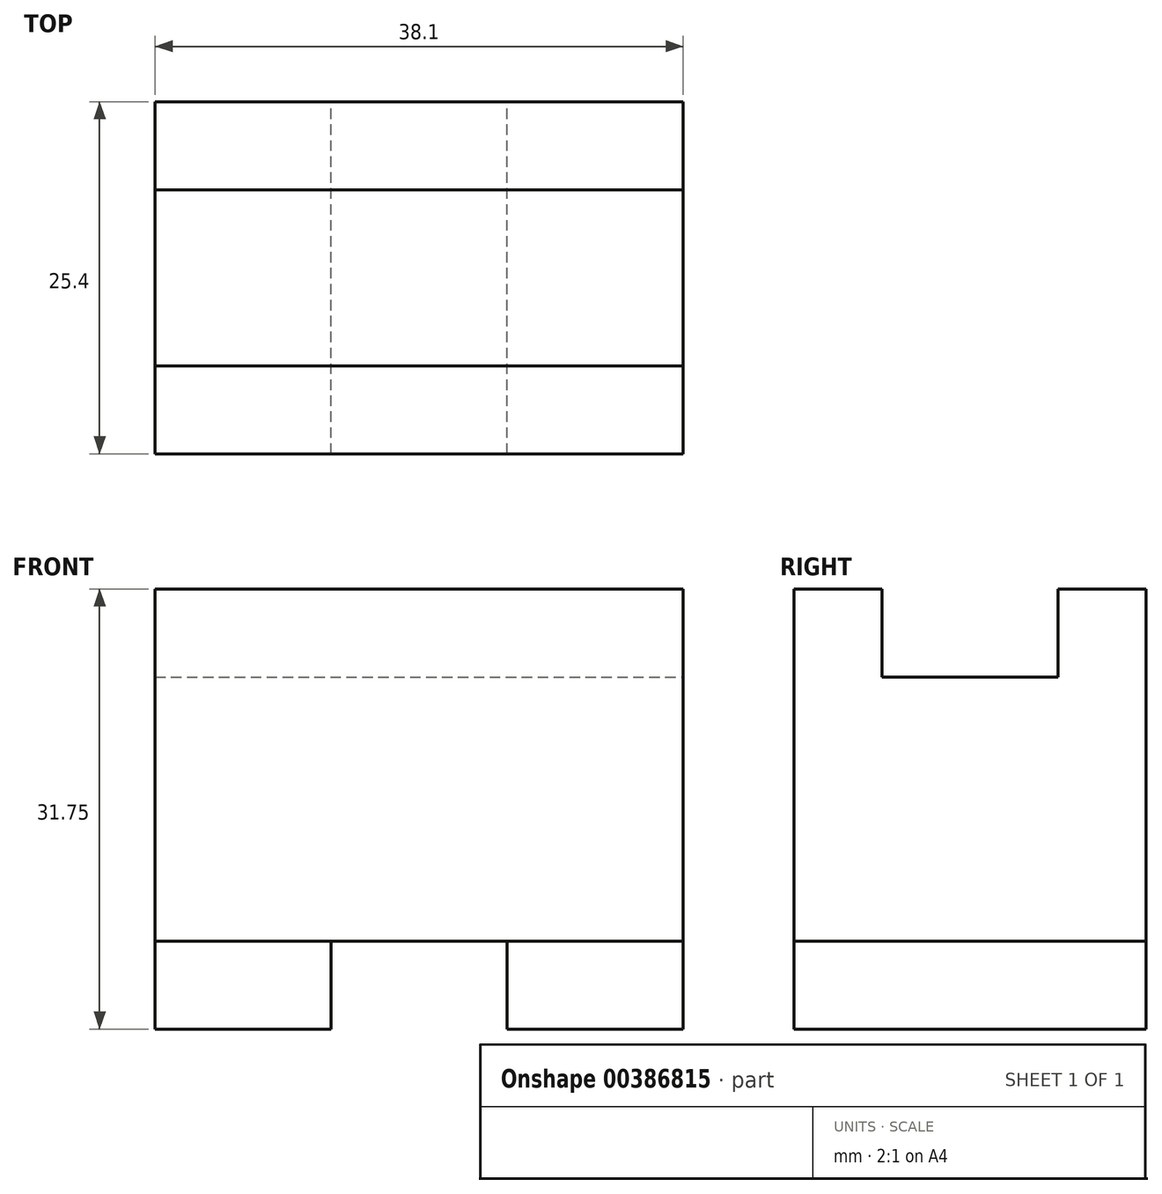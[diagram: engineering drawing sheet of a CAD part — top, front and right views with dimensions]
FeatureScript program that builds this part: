
annotation { "Feature Type Name" : "Feature", "Feature Type Description" : "" }
export const myFeature = defineFeature(function(context is Context, id is Id, definition is map)
    precondition{}
    {
        {
            var Q0;
            Q0=qCreatedBy(makeId("Top.planeOp"),FACE);
            var sketch = newSketch(context, id + "F0", { "sketchPlane" : qUnion([Q0])});
            skLineSegment(sketch, "E0", {"start": v(0, 0) * mm, "end": v(38.1, 0) * mm});
            skLineSegment(sketch, "E1", {"start": v(38.1, 0) * mm, "end": v(38.1, 25.4) * mm});
            skLineSegment(sketch, "E2", {"start": v(38.1, 25.4) * mm, "end": v(0, 25.4) * mm});
            skLineSegment(sketch, "E3", {"start": v(0, 25.4) * mm, "end": v(0, 0) * mm});
            skLineSegment(sketch, "E4", {"start": v(38.1, 0) * mm, "end": v(25.4, 0) * mm});
            skLineSegment(sketch, "E5", {"start": v(25.4, 0) * mm, "end": v(25.4, 25.4) * mm});
            skLineSegment(sketch, "E6", {"start": v(25.4, 25.4) * mm, "end": v(38.1, 25.4) * mm});
            skLineSegment(sketch, "E7", {"start": v(0, 0) * mm, "end": v(12.7, 0) * mm});
            skLineSegment(sketch, "E8", {"start": v(12.7, 0) * mm, "end": v(12.7, 25.4) * mm});
            skLineSegment(sketch, "E9", {"start": v(12.7, 25.4) * mm, "end": v(0, 25.4) * mm});
            skSolve(sketch);
        }
        {
            var Q0;
            Q0=makeQuery(id+"F0.imprint","IMPRINT",FACE,{"disambiguationData":[TD([[makeQuery(id+"F0.imprint","IMPRINT",EDGE,{"derivedFrom":sQuery(id+"F0.wireOp",EDGE,"E1")}),1.0]])]});
            var Q1;
            Q1=makeQuery(id+"F0.imprint","IMPRINT",FACE,{"disambiguationData":[TD([[makeQuery(id+"F0.imprint","IMPRINT",EDGE,{"derivedFrom":sQuery(id+"F0.wireOp",EDGE,"E3")}),1.0]])]});
            extrude(context, id + "F1", {"entities" : qUnion([Q0, Q1]), "depth" : 6.35 * mm});
        }
        {
            var Q0;
            Q0=qCreatedBy(makeId("Top.planeOp"),FACE);
            var sketch = newSketch(context, id + "F2", { "sketchPlane" : qUnion([Q0])});
            skLineSegment(sketch, "E10", {"start": v(0, 0) * mm, "end": v(38.1, 0) * mm});
            skLineSegment(sketch, "E11", {"start": v(38.1, 0) * mm, "end": v(38.1, 25.4) * mm});
            skLineSegment(sketch, "E12", {"start": v(38.1, 25.4) * mm, "end": v(0, 25.4) * mm});
            skLineSegment(sketch, "E13", {"start": v(0, 25.4) * mm, "end": v(0, 0) * mm});
            skSolve(sketch);
        }
        {
            var Q0;
            Q0=makeQuery(id+"F1.opExtrude","CAP_FACE",FACE,{"disambiguationData":[OSD([sQuery(id+"F0.wireOp",EDGE,"E3"),sQuery(id+"F0.wireOp",EDGE,"E7"),sQuery(id+"F0.wireOp",EDGE,"E8"),sQuery(id+"F0.wireOp",EDGE,"E9")])],"isStart":false});
            var sketch = newSketch(context, id + "F3", { "sketchPlane" : qUnion([Q0])});
            skLineSegment(sketch, "E14", {"start": v(0, 25.4) * mm, "end": v(38.1, 25.4) * mm});
            skLineSegment(sketch, "E15", {"start": v(38.1, 25.4) * mm, "end": v(38.1, 0) * mm});
            skLineSegment(sketch, "E16", {"start": v(38.1, 0) * mm, "end": v(0, 0) * mm});
            skLineSegment(sketch, "E17", {"start": v(0, 0) * mm, "end": v(0, 25.4) * mm});
            skSolve(sketch);
        }
        {
            var Q0;
            {var subQ2=sQuery(id+"F3.wireOp",EDGE,"E15");Q0=makeQuery(id+"F3.imprint","IMPRINT",FACE,{"disambiguationData":[TD([[makeQuery(id+"F3.imprint","IMPRINT",EDGE,{"derivedFrom":subQ2}),-1.0]])]});}
            var Q1;
            {var subQ2=sQuery(id+"F3.wireOp",EDGE,"E17");Q1=makeQuery(id+"F3.imprint","IMPRINT",FACE,{"disambiguationData":[TD([[makeQuery(id+"F3.imprint","IMPRINT",EDGE,{"derivedFrom":subQ2}),1.0]])]});}
            extrude(context, id + "F4", {"entities" : qUnion([Q0, Q1]), "depth" : 19.05 * mm});
        }
        {
            var Q0;
            Q0=makeQuery(id+"F4.opExtrude","CAP_FACE",FACE,{"disambiguationData":[OSD([sQuery(id+"F3.wireOp",EDGE,"E14"),sQuery(id+"F3.wireOp",EDGE,"E15"),sQuery(id+"F3.wireOp",EDGE,"E16"),sQuery(id+"F3.wireOp",EDGE,"E17")])],"isStart":false});
            var sketch = newSketch(context, id + "F5", { "sketchPlane" : qUnion([Q0])});
            skLineSegment(sketch, "E18", {"start": v(0, 25.4) * mm, "end": v(0, 19.05) * mm});
            skLineSegment(sketch, "E19", {"start": v(0, 19.05) * mm, "end": v(38.1, 19.05) * mm});
            skLineSegment(sketch, "E20", {"start": v(38.1, 19.05) * mm, "end": v(38.1, 25.4) * mm});
            skLineSegment(sketch, "E21", {"start": v(38.1, 25.4) * mm, "end": v(0, 25.4) * mm});
            skLineSegment(sketch, "E22", {"start": v(0, 0) * mm, "end": v(0, 6.34) * mm});
            skLineSegment(sketch, "E23", {"start": v(0, 6.34) * mm, "end": v(38.1, 6.34) * mm});
            skLineSegment(sketch, "E24", {"start": v(38.1, 6.34) * mm, "end": v(38.1, 0) * mm});
            skLineSegment(sketch, "E25", {"start": v(38.1, 0) * mm, "end": v(0, 0) * mm});
            skSolve(sketch);
        }
        {
            var Q0;
            Q0=makeQuery(id+"F5.imprint","IMPRINT",FACE,{"disambiguationData":[TD([[makeQuery(id+"F5.imprint","IMPRINT",EDGE,{"derivedFrom":sQuery(id+"F5.wireOp",EDGE,"E22")}),1.0]])]});
            extrude(context, id + "F6", {"entities" : qUnion([Q0]), "operationType" : NewBodyOperationType.ADD, "depth" : 6.35 * mm});
        }
        {
            var Q0;
            Q0=makeQuery(id+"F4.opExtrude","CAP_FACE",FACE,{"disambiguationData":[OSD([sQuery(id+"F3.wireOp",EDGE,"E14"),sQuery(id+"F3.wireOp",EDGE,"E15"),sQuery(id+"F3.wireOp",EDGE,"E16"),sQuery(id+"F3.wireOp",EDGE,"E17")])],"isStart":false});
            var sketch = newSketch(context, id + "F7", { "sketchPlane" : qUnion([Q0])});
            skLineSegment(sketch, "E26", {"start": v(0, 25.4) * mm, "end": v(0, 19.05) * mm});
            skLineSegment(sketch, "E27", {"start": v(0, 19.05) * mm, "end": v(38.1, 19.05) * mm});
            skLineSegment(sketch, "E28", {"start": v(38.1, 19.05) * mm, "end": v(38.1, 25.4) * mm});
            skLineSegment(sketch, "E29", {"start": v(38.1, 25.4) * mm, "end": v(0, 25.4) * mm});
            skSolve(sketch);
        }
        {
            var Q0;
            Q0=makeQuery(id+"F7.imprint","IMPRINT",FACE,{"disambiguationData":[TD([[makeQuery(id+"F7.imprint","IMPRINT",EDGE,{"derivedFrom":sQuery(id+"F7.wireOp",EDGE,"E26")}),1.0]])]});
            extrude(context, id + "F8", {"entities" : qUnion([Q0]), "operationType" : NewBodyOperationType.ADD, "depth" : 6.35 * mm});
        }
    });
